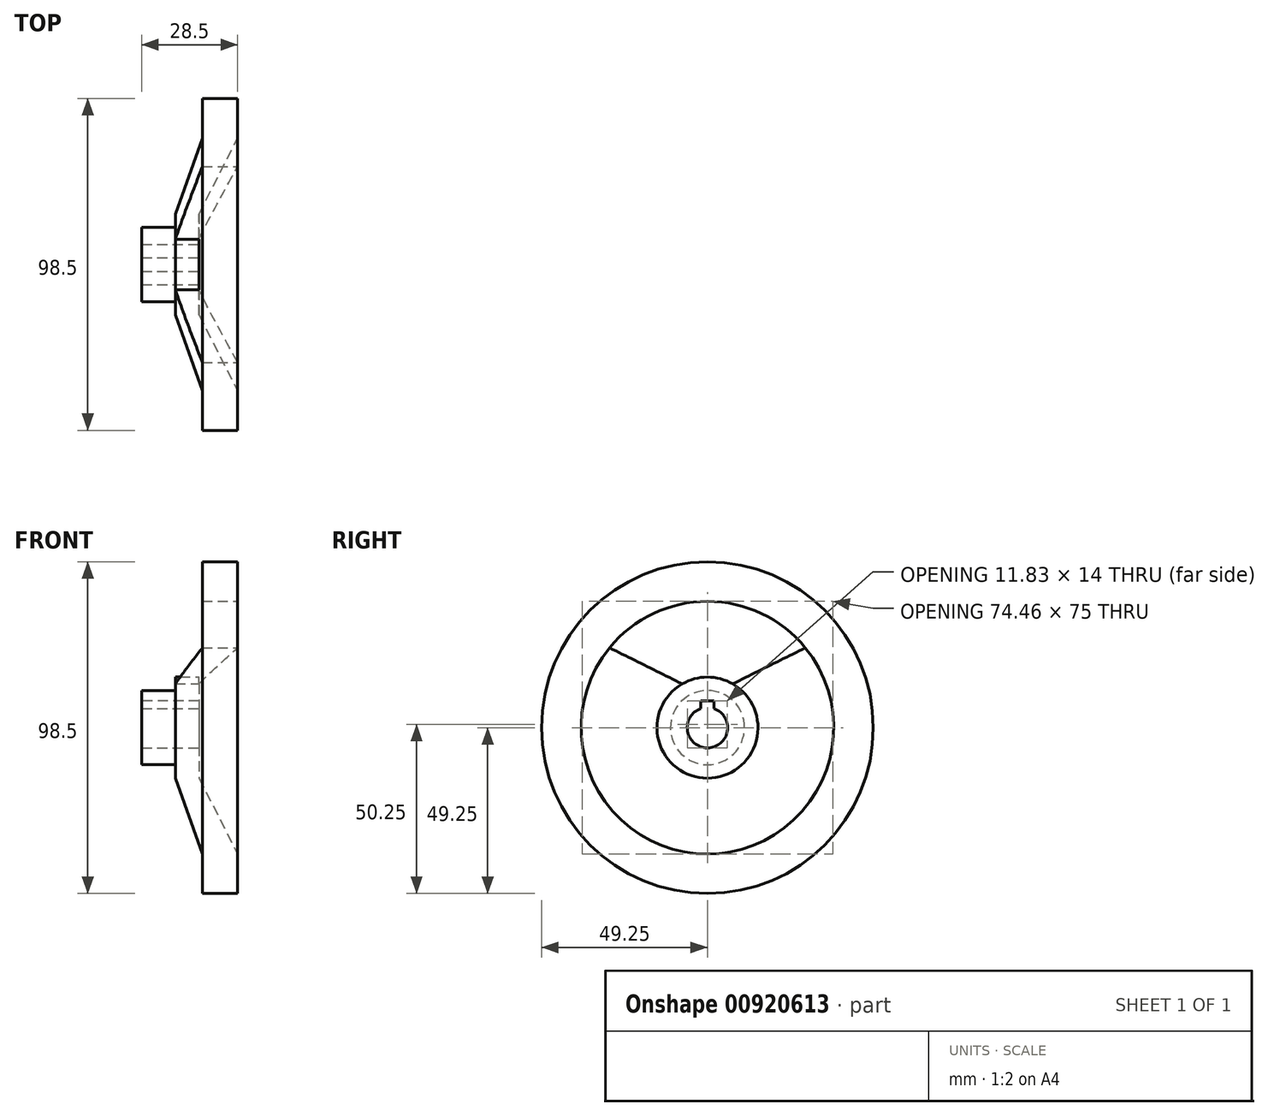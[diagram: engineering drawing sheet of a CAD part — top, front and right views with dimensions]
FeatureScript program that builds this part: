
annotation { "Feature Type Name" : "Feature", "Feature Type Description" : "" }
export const myFeature = defineFeature(function(context is Context, id is Id, definition is map)
    precondition{}
    {
        {
            var Q0;
            Q0=qCreatedBy(makeId("Front.planeOp"),FACE);
            var sketch = newSketch(context, id + "F0", { "sketchPlane" : qUnion([Q0])});
            skLineSegment(sketch, "E0", {"start": v(0, 0) * mm, "end": v(-19.33, 0) * mm, "construction": true});
            skLineSegment(sketch, "E1", {"start": v(0, 6) * mm, "end": v(17, 6) * mm});
            skLineSegment(sketch, "E2", {"start": v(0, 6) * mm, "end": v(0, 11) * mm});
            skLineSegment(sketch, "E3", {"start": v(0, 11) * mm, "end": v(10, 11) * mm});
            skLineSegment(sketch, "E4", {"start": v(10, 11) * mm, "end": v(10, 15) * mm});
            skLineSegment(sketch, "E5", {"start": v(10, 15) * mm, "end": v(17, 15) * mm, "construction": true});
            skLineSegment(sketch, "E6", {"start": v(17, 6) * mm, "end": v(17, 15) * mm});
            skLineSegment(sketch, "E7.bottom", {"start": v(18, 49.25) * mm, "end": v(28.5, 49.25) * mm});
            skLineSegment(sketch, "E7.top", {"start": v(18, 37.5) * mm, "end": v(28.5, 37.5) * mm, "construction": true});
            skLineSegment(sketch, "E7.left", {"start": v(18, 49.25) * mm, "end": v(18, 37.5) * mm});
            skLineSegment(sketch, "E7.right", {"start": v(28.5, 49.25) * mm, "end": v(28.5, 37.5) * mm});
            skLineSegment(sketch, "E8", {"start": v(17, 15) * mm, "end": v(28.5, 37.5) * mm});
            skLineSegment(sketch, "E9", {"start": v(10, 15) * mm, "end": v(18, 37.5) * mm});
            skSolve(sketch);
        }
        {
            var Q0;
            Q0=makeQuery(id+"F0.imprint","IMPRINT",FACE,{"disambiguationData":[TD([[makeQuery(id+"F0.imprint","IMPRINT",EDGE,{"derivedFrom":sQuery(id+"F0.wireOp",EDGE,"E7.bottom")}),-1.0]])]});
            var Q1;
            Q1=makeQuery(id+"F0.imprint","IMPRINT",FACE,{"disambiguationData":[TD([[makeQuery(id+"F0.imprint","IMPRINT",EDGE,{"derivedFrom":sQuery(id+"F0.wireOp",EDGE,"E1")}),1.0]])]});
            var Q2;
            Q2=sQuery(id+"F0.wireOp",EDGE,"E0");
            revolve(context, id + "F1", {"surfaceOperationType" : NewSurfaceOperationType.NEW, "entities" : qUnion([Q0, Q1]), "axis" : qUnion([Q2]), "revolveType" : RevolveType.FULL});
        }
        {
            var Q0;
            Q0=qCreatedBy(makeId("Right.planeOp"),FACE);
            var sketch = newSketch(context, id + "F2", { "sketchPlane" : qUnion([Q0])});
            skLineSegment(sketch, "E10.bottom", {"start": v(2, 0) * mm, "end": v(-2, 0) * mm});
            skLineSegment(sketch, "E10.top", {"start": v(2, 8) * mm, "end": v(-2, 8) * mm});
            skLineSegment(sketch, "E10.left", {"start": v(2, 0) * mm, "end": v(2, 8) * mm});
            skLineSegment(sketch, "E10.right", {"start": v(-2, 0) * mm, "end": v(-2, 8) * mm});
            skSolve(sketch);
        }
        {
            var Q0;
            Q0=makeQuery(id+"F2.imprint","IMPRINT",FACE,{"disambiguationData":[TD([[makeQuery(id+"F2.imprint","IMPRINT",EDGE,{"derivedFrom":sQuery(id+"F2.wireOp",EDGE,"E10.bottom")}),-1.0]])]});
            extrude(context, id + "F3", {"entities" : qUnion([Q0]), "operationType" : NewBodyOperationType.REMOVE, "depth" : 25 * mm, "offsetDistance" : 25 * mm});
        }
        {
            var Q0;
            Q0=makeQuery(id+"F1.opRevolve","SWEPT_FACE",FACE,{"disambiguationData":[OSD([sQuery(id+"F0.wireOp",EDGE,"E7.right")])]});
            var sketch = newSketch(context, id + "F4", { "sketchPlane" : qUnion([Q0])});
            skArc(sketch, "E11.0", {"start": v(29.06, 23.7) * mm, "mid": v(0, 37.5) * mm, "end": v(-29.06, 23.7) * mm});
            skArc(sketch, "E12.0", {"start": v(7.5, 13) * mm, "mid": v(0, 15) * mm, "end": v(-7.5, 13) * mm});
            skLineSegment(sketch, "E13", {"start": v(0, 0) * mm, "end": v(-32.48, 18.75) * mm, "construction": true});
            skLineSegment(sketch, "E14", {"start": v(0, 0) * mm, "end": v(32.48, 18.75) * mm, "construction": true});
            skLineSegment(sketch, "E15", {"start": v(-29.06, 23.7) * mm, "end": v(-7.5, 13) * mm});
            skLineSegment(sketch, "E16", {"start": v(7.5, 13) * mm, "end": v(29.06, 23.7) * mm});
            skSolve(sketch);
        }
        {
            var Q0;
            Q0=makeQuery(id+"F4.imprint","IMPRINT",FACE,{"disambiguationData":[TD([[makeQuery(id+"F4.imprint","IMPRINT",EDGE,{"derivedFrom":sQuery(id+"F4.wireOp",EDGE,"E11.0")}),1.0]])]});
            extrude(context, id + "F5", {"entities" : qUnion([Q0]), "operationType" : NewBodyOperationType.REMOVE, "endBound" : BoundingType.THROUGH_ALL, "oppositeDirection" : true, "depth" : 25 * mm, "offsetDistance" : 25 * mm});
        }
    });
